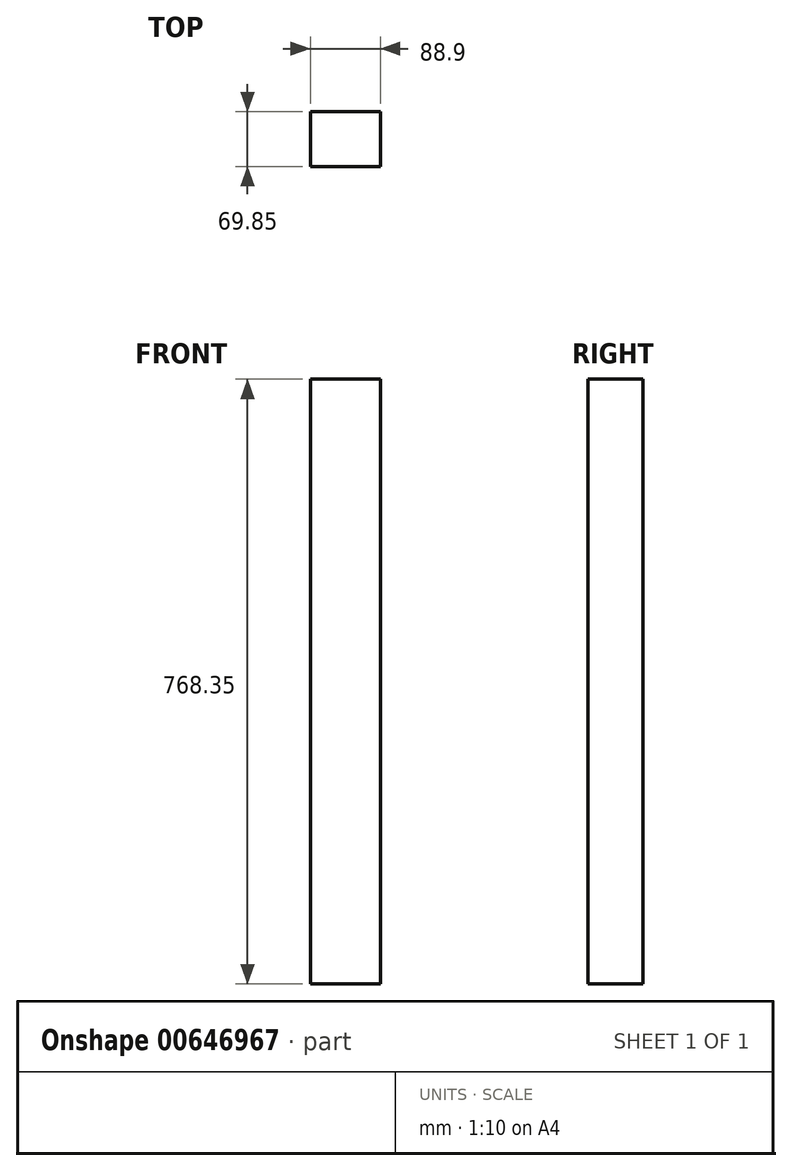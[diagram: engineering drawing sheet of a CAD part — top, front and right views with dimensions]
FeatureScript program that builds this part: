
annotation { "Feature Type Name" : "Feature", "Feature Type Description" : "" }
export const myFeature = defineFeature(function(context is Context, id is Id, definition is map)
    precondition{}
    {
        {
            var Q0;
            Q0=qCreatedBy(makeId("Front.planeOp"),FACE);
            var sketch = newSketch(context, id + "F0", { "sketchPlane" : qUnion([Q0])});
            skLineSegment(sketch, "E0", {"start": v(-38.02, 387.84) * mm, "end": v(-38.02, -380.51) * mm});
            skLineSegment(sketch, "E1", {"start": v(-38.02, -380.51) * mm, "end": v(50.88, -380.51) * mm});
            skLineSegment(sketch, "E2", {"start": v(-38.02, 387.84) * mm, "end": v(50.88, 387.84) * mm});
            skLineSegment(sketch, "E3", {"start": v(50.88, 387.84) * mm, "end": v(50.88, -380.51) * mm});
            skSolve(sketch);
        }
        {
            var Q0;
            Q0=makeQuery(id+"F0.imprint","IMPRINT",FACE,{"disambiguationData":[TD([[makeQuery(id+"F0.imprint","IMPRINT",EDGE,{"derivedFrom":sQuery(id+"F0.wireOp",EDGE,"E0")}),1.0]])]});
            extrude(context, id + "F1", {"entities" : qUnion([Q0]), "depth" : 69.85 * mm, "offsetDistance" : 25.4 * mm});
        }
    });
